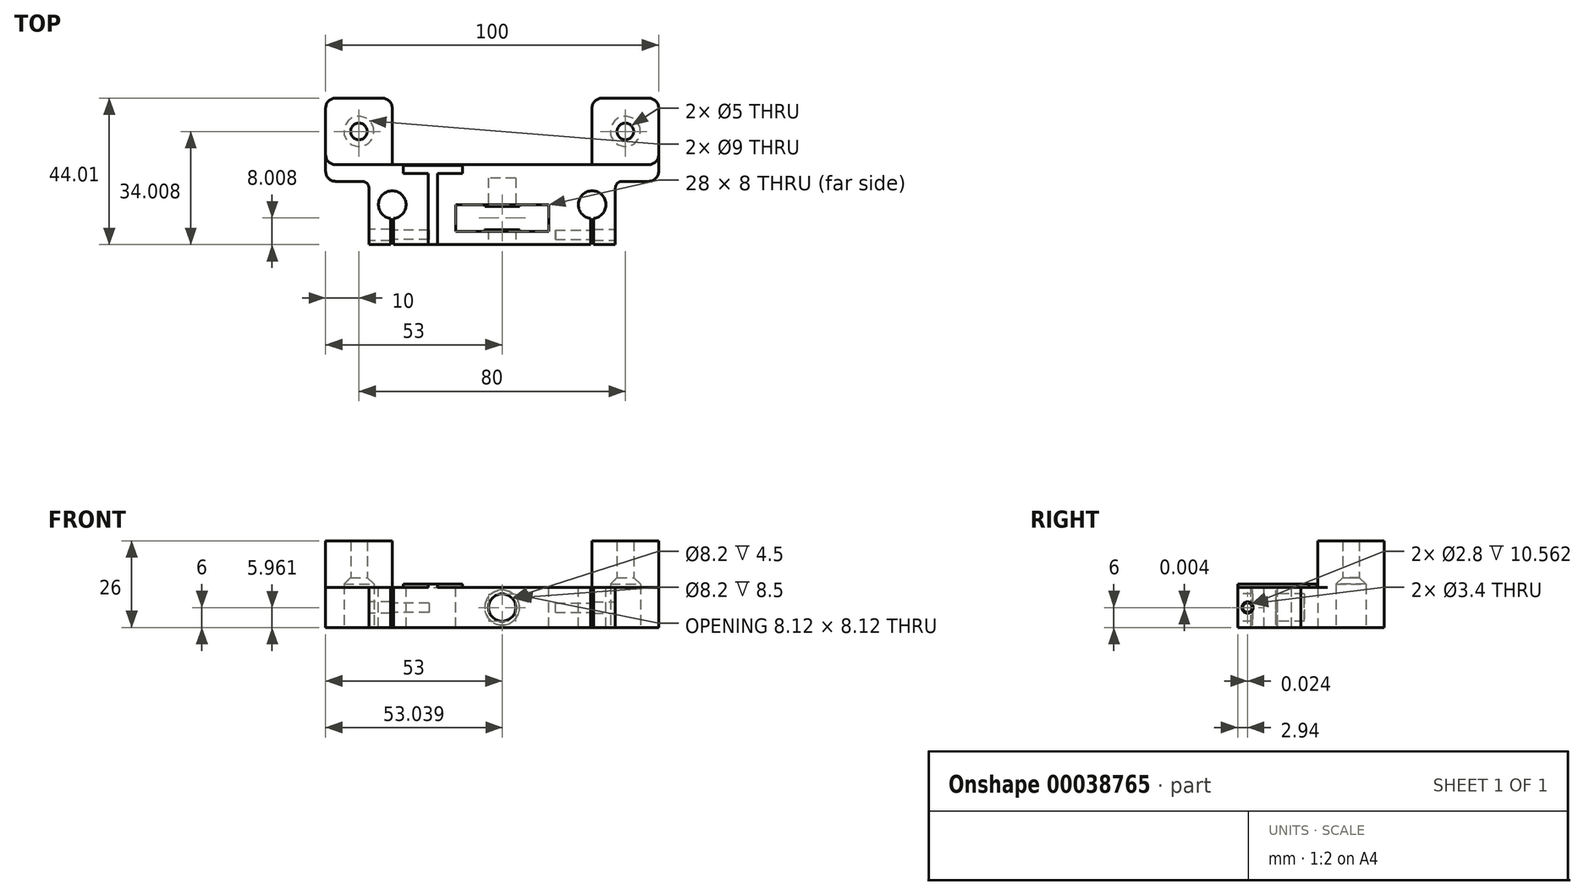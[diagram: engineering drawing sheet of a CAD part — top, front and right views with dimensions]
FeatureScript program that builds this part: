
annotation { "Feature Type Name" : "Feature", "Feature Type Description" : "" }
export const myFeature = defineFeature(function(context is Context, id is Id, definition is map)
    precondition{}
    {
        {
            var Q0;
            Q0=qCreatedBy(makeId("Top.planeOp"),FACE);
            var sketch = newSketch(context, id + "F0", { "sketchPlane" : qUnion([Q0])});
            skLineSegment(sketch, "E0", {"start": v(-46.35, 12.3) * mm, "end": v(53.65, 12.3) * mm});
            skLineSegment(sketch, "E1", {"start": v(53.65, 12.3) * mm, "end": v(53.65, 7.3) * mm});
            skLineSegment(sketch, "E2", {"start": v(53.65, 7.3) * mm, "end": v(40.65, 7.3) * mm});
            skLineSegment(sketch, "E3", {"start": v(40.65, 7.3) * mm, "end": v(40.65, -11.7) * mm});
            skLineSegment(sketch, "E4", {"start": v(40.65, -11.7) * mm, "end": v(-33.35, -11.7) * mm});
            skLineSegment(sketch, "E5", {"start": v(-33.35, -11.7) * mm, "end": v(-33.35, 7.3) * mm});
            skLineSegment(sketch, "E6", {"start": v(-33.35, 7.3) * mm, "end": v(-46.35, 7.3) * mm});
            skLineSegment(sketch, "E7", {"start": v(-46.35, 7.3) * mm, "end": v(-46.35, 12.3) * mm});
            skSolve(sketch);
        }
        {
            var Q0;
            Q0=qSketchRegion(id+"F0",true);
            extrude(context, id + "F1", {"entities" : qUnion([Q0]), "depth" : 12 * mm});
        }
        {
            var Q0;
            Q0=makeQuery(id+"F1.opExtrude","CAP_FACE",FACE,{"disambiguationData":[OSD([sQuery(id+"F0.wireOp",EDGE,"E0"),sQuery(id+"F0.wireOp",EDGE,"E1"),sQuery(id+"F0.wireOp",EDGE,"E2"),sQuery(id+"F0.wireOp",EDGE,"E3"),sQuery(id+"F0.wireOp",EDGE,"E4"),sQuery(id+"F0.wireOp",EDGE,"E5"),sQuery(id+"F0.wireOp",EDGE,"E6"),sQuery(id+"F0.wireOp",EDGE,"E7")])],"isStart":false});
            var sketch = newSketch(context, id + "F2", { "sketchPlane" : qUnion([Q0])});
            skCircle(sketch, "E8", {"center": v(-26.35, 0.3) * mm, "radius": 4.15 * mm});
            skCircle(sketch, "E9", {"center": v(33.65, 0.3) * mm, "radius": 4.15 * mm});
            skPoint(sketch, "E10", {"position": v(3.65, 12.3) * mm});
            skLineSegment(sketch, "E11.bottom", {"start": v(33.21, -3.01) * mm, "end": v(34.09, -3.01) * mm});
            skLineSegment(sketch, "E11.top", {"start": v(33.21, -12.27) * mm, "end": v(34.09, -12.27) * mm});
            skLineSegment(sketch, "E11.left", {"start": v(33.21, -3.01) * mm, "end": v(33.21, -12.27) * mm});
            skLineSegment(sketch, "E11.right", {"start": v(34.09, -3.01) * mm, "end": v(34.09, -12.27) * mm});
            skPoint(sketch, "E12", {"position": v(33.65, -3.01) * mm});
            skLineSegment(sketch, "E13", {"start": v(3.65, 12.3) * mm, "end": v(3.65, -11.7) * mm, "construction": true});
            skLineSegment(sketch, "E14.MirrorCS", {"start": v(-25.91, -12.27) * mm, "end": v(-26.79, -12.27) * mm});
            skLineSegment(sketch, "E15.MirrorCS", {"start": v(-26.79, -3.01) * mm, "end": v(-26.79, -12.27) * mm});
            skLineSegment(sketch, "E16.MirrorCS", {"start": v(-25.91, -3.01) * mm, "end": v(-26.79, -3.01) * mm});
            skLineSegment(sketch, "E17.MirrorCS", {"start": v(-25.91, -3.01) * mm, "end": v(-25.91, -12.27) * mm});
            skSolve(sketch);
        }
        {
            var Q0;
            Q0=qSketchRegion(id+"F2",true);
            var Q1;
            {var subQ3=sQuery(id+"F2.wireOp",EDGE,"E11.bottom");Q1=makeQuery(id+"F2.imprint","IMPRINT",FACE,{"disambiguationData":[TD([[makeQuery(id+"F2.imprint","IMPRINT",EDGE,{"derivedFrom":subQ3}),-1.0]])]});}
            var Q2;
            {var subQ3=sQuery(id+"F2.wireOp",EDGE,"E16.MirrorCS");Q2=makeQuery(id+"F2.imprint","IMPRINT",FACE,{"disambiguationData":[TD([[makeQuery(id+"F2.imprint","IMPRINT",EDGE,{"derivedFrom":subQ3}),1.0]])]});}
            extrude(context, id + "F3", {"entities" : qUnion([Q0, Q1, Q2]), "operationType" : NewBodyOperationType.REMOVE, "endBound" : BoundingType.THROUGH_ALL, "oppositeDirection" : true, "depth" : 25 * mm});
        }
        {
            var Q0;
            Q0=makeQuery(id+"F1.opExtrude","SWEPT_FACE",FACE,{"disambiguationData":[OSD([sQuery(id+"F0.wireOp",EDGE,"E4")])]});
            var sketch = newSketch(context, id + "F4", { "sketchPlane" : qUnion([Q0])});
            skLineSegment(sketch, "E18", {"start": v(-33.35, 6) * mm, "end": v(40.65, 6) * mm, "construction": true});
            skCircle(sketch, "E19", {"center": v(6.65, 6) * mm, "radius": 4.1 * mm});
            skSolve(sketch);
        }
        {
            var Q0;
            Q0=qSketchRegion(id+"F4",true);
            extrude(context, id + "F5", {"entities" : qUnion([Q0]), "operationType" : NewBodyOperationType.REMOVE, "oppositeDirection" : true, "depth" : 20 * mm});
        }
        {
            var Q0;
            Q0=makeQuery(id+"F1.opExtrude","CAP_FACE",FACE,{"disambiguationData":[OSD([sQuery(id+"F0.wireOp",EDGE,"E0"),sQuery(id+"F0.wireOp",EDGE,"E1"),sQuery(id+"F0.wireOp",EDGE,"E2"),sQuery(id+"F0.wireOp",EDGE,"E3"),sQuery(id+"F0.wireOp",EDGE,"E4"),sQuery(id+"F0.wireOp",EDGE,"E5"),sQuery(id+"F0.wireOp",EDGE,"E6"),sQuery(id+"F0.wireOp",EDGE,"E7")])],"isStart":false});
            var sketch = newSketch(context, id + "F6", { "sketchPlane" : qUnion([Q0])});
            skLineSegment(sketch, "E20.bottom", {"start": v(-7.35, 0.3) * mm, "end": v(20.65, 0.3) * mm});
            skLineSegment(sketch, "E20.top", {"start": v(-7.35, -7.7) * mm, "end": v(20.65, -7.7) * mm});
            skLineSegment(sketch, "E20.left", {"start": v(-7.35, 0.3) * mm, "end": v(-7.35, -7.7) * mm});
            skLineSegment(sketch, "E20.right", {"start": v(20.65, 0.3) * mm, "end": v(20.65, -7.7) * mm});
            skLineSegment(sketch, "E21", {"start": v(6.65, 12.3) * mm, "end": v(6.65, -11.7) * mm, "construction": true});
            skLineSegment(sketch, "E22", {"start": v(6.65, 0.3) * mm, "end": v(6.65, -7.7) * mm});
            skSolve(sketch);
        }
        {
            var Q0;
            Q0=qSketchRegion(id+"F6",true);
            extrude(context, id + "F7", {"entities" : qUnion([Q0]), "operationType" : NewBodyOperationType.REMOVE, "endBound" : BoundingType.THROUGH_ALL, "oppositeDirection" : true, "depth" : 25 * mm});
        }
        {
            var Q0;
            Q0=makeQuery(id+"F7.boolean.opBoolean","COPY",FACE,{"derivedFrom":makeQuery(id+"F7.opExtrude","SWEPT_FACE",FACE,{"disambiguationData":[OSD([sQuery(id+"F6.wireOp",EDGE,"E20.bottom")])]})});
            var sketch = newSketch(context, id + "F8", { "sketchPlane" : qUnion([Q0])});
            skCircle(sketch, "E23", {"center": v(6.65, 6) * mm, "radius": 5.2 * mm});
            skSolve(sketch);
        }
        {
            var Q0;
            Q0=makeQuery(id+"F8.imprint","IMPRINT",FACE,{"disambiguationData":[TD([[makeQuery(id+"F8.imprint","IMPRINT",EDGE,{"derivedFrom":sQuery(id+"F8.wireOp",EDGE,"E23")}),1.0]])]});
            extrude(context, id + "F9", {"entities" : qUnion([Q0]), "operationType" : NewBodyOperationType.ADD, "depth" : 0.5 * mm});
        }
        {
            var Q0;
            Q0=makeQuery(id+"F7.boolean.opBoolean","COPY",FACE,{"derivedFrom":makeQuery(id+"F7.opExtrude","SWEPT_FACE",FACE,{"disambiguationData":[OSD([sQuery(id+"F6.wireOp",EDGE,"E20.top")])]})});
            var sketch = newSketch(context, id + "F10", { "sketchPlane" : qUnion([Q0])});
            skCircle(sketch, "E24", {"center": v(-6.65, 6) * mm, "radius": 5.25 * mm});
            skSolve(sketch);
        }
        {
            var Q0;
            Q0=makeQuery(id+"F10.imprint","IMPRINT",FACE,{"disambiguationData":[TD([[makeQuery(id+"F10.imprint","IMPRINT",EDGE,{"derivedFrom":sQuery(id+"F10.wireOp",EDGE,"E24")}),1.0]])]});
            extrude(context, id + "F11", {"entities" : qUnion([Q0]), "operationType" : NewBodyOperationType.ADD, "depth" : 0.5 * mm});
        }
        {
            var Q0;
            Q0=makeQuery(id+"F1.opExtrude","CAP_FACE",FACE,{"disambiguationData":[OSD([sQuery(id+"F0.wireOp",EDGE,"E0"),sQuery(id+"F0.wireOp",EDGE,"E1"),sQuery(id+"F0.wireOp",EDGE,"E2"),sQuery(id+"F0.wireOp",EDGE,"E3"),sQuery(id+"F0.wireOp",EDGE,"E4"),sQuery(id+"F0.wireOp",EDGE,"E5"),sQuery(id+"F0.wireOp",EDGE,"E6"),sQuery(id+"F0.wireOp",EDGE,"E7")])],"isStart":false});
            var sketch = newSketch(context, id + "F12", { "sketchPlane" : qUnion([Q0])});
            skText(sketch, "E25", { "text": "T", "fontName": "OpenSans-Regular.ttf"});
            const initialGuessF12  = {"E25": [-0.02337, -0.0117, 1, 0, 0.024]};
            skSetInitialGuess(sketch, initialGuessF12);
            skSolve(sketch);
        }
        {
            var Q0;
            Q0=qSketchRegion(id+"F12",true);
            extrude(context, id + "F13", {"entities" : qUnion([Q0]), "operationType" : NewBodyOperationType.ADD, "depth" : 1 * mm});
        }
        {
            var Q0;
            Q0=makeQuery(id+"F1.opExtrude","SWEPT_FACE",FACE,{"disambiguationData":[OSD([sQuery(id+"F0.wireOp",EDGE,"E3")])]});
            var sketch = newSketch(context, id + "F14", { "sketchPlane" : qUnion([Q0])});
            skCircle(sketch, "E26", {"center": v(-8.74, 6) * mm, "radius": 1.7 * mm});
            skCircle(sketch, "E27", {"center": v(-8.74, 6) * mm, "radius": 1.4 * mm});
            skLineSegment(sketch, "E28", {"start": v(-11.7, 6) * mm, "end": v(-3.84, 6) * mm, "construction": true});
            skSolve(sketch);
        }
        {
            var Q0;
            Q0=makeQuery(id+"F14.imprint","IMPRINT",FACE,{"disambiguationData":[TD([[makeQuery(id+"F14.imprint","IMPRINT",EDGE,{"derivedFrom":sQuery(id+"F14.wireOp",EDGE,"E27")}),1.0]])]});
            extrude(context, id + "F15", {"entities" : qUnion([Q0]), "operationType" : NewBodyOperationType.REMOVE, "oppositeDirection" : true, "depth" : 18 * mm});
        }
        {
            var Q0;
            Q0=makeQuery(id+"F14.imprint","IMPRINT",FACE,{"disambiguationData":[TD([[makeQuery(id+"F14.imprint","IMPRINT",EDGE,{"derivedFrom":sQuery(id+"F14.wireOp",EDGE,"E27")}),1.0]])]});
            var Q1;
            Q1=makeQuery(id+"F14.imprint","IMPRINT",FACE,{"disambiguationData":[TD([[makeQuery(id+"F14.imprint","IMPRINT",EDGE,{"derivedFrom":sQuery(id+"F14.wireOp",EDGE,"E26")}),1.0]])]});
            extrude(context, id + "F16", {"entities" : qUnion([Q0, Q1]), "operationType" : NewBodyOperationType.REMOVE, "endBound" : BoundingType.UP_TO_NEXT, "oppositeDirection" : true, "depth" : 7 * mm});
        }
        {
            var Q0;
            Q0=makeQuery(id+"F1.opExtrude","SWEPT_EDGE",EDGE,{"disambiguationData":[OSD([sQuery(id+"F0.wireOp",EDGE,"E2"),sQuery(id+"F0.wireOp",EDGE,"E3")])]});
            fillet(context, id + "F17", {"entities" : qUnion([Q0]), "radius" : 2 * mm, "tangentPropagation" : true, "allowEdgeOverflow" : false});
        }
        {
            var Q0;
            Q0=makeQuery(id+"F1.opExtrude","SWEPT_FACE",FACE,{"disambiguationData":[OSD([sQuery(id+"F0.wireOp",EDGE,"E5")])]});
            var sketch = newSketch(context, id + "F18", { "sketchPlane" : qUnion([Q0])});
            skCircle(sketch, "E29", {"center": v(8.76, 6) * mm, "radius": 1.7 * mm});
            skCircle(sketch, "E30", {"center": v(8.76, 6) * mm, "radius": 1.4 * mm});
            skLineSegment(sketch, "E31", {"start": v(8.76, 0) * mm, "end": v(8.76, 12) * mm, "construction": true});
            skSolve(sketch);
        }
        {
            var Q0;
            Q0=makeQuery(id+"F18.imprint","IMPRINT",FACE,{"disambiguationData":[TD([[makeQuery(id+"F18.imprint","IMPRINT",EDGE,{"derivedFrom":sQuery(id+"F18.wireOp",EDGE,"E30")}),1.0]])]});
            extrude(context, id + "F19", {"entities" : qUnion([Q0]), "operationType" : NewBodyOperationType.REMOVE, "oppositeDirection" : true, "depth" : 18 * mm});
        }
        {
            var Q0;
            Q0=makeQuery(id+"F18.imprint","IMPRINT",FACE,{"disambiguationData":[TD([[makeQuery(id+"F18.imprint","IMPRINT",EDGE,{"derivedFrom":sQuery(id+"F18.wireOp",EDGE,"E30")}),1.0]])]});
            var Q1;
            Q1=makeQuery(id+"F18.imprint","IMPRINT",FACE,{"disambiguationData":[TD([[makeQuery(id+"F18.imprint","IMPRINT",EDGE,{"derivedFrom":sQuery(id+"F18.wireOp",EDGE,"E29")}),1.0]])]});
            extrude(context, id + "F20", {"entities" : qUnion([Q0, Q1]), "operationType" : NewBodyOperationType.REMOVE, "endBound" : BoundingType.UP_TO_NEXT, "oppositeDirection" : true, "depth" : 25 * mm});
        }
        {
            var Q0;
            Q0=makeQuery(id+"F1.opExtrude","SWEPT_EDGE",EDGE,{"disambiguationData":[OSD([sQuery(id+"F0.wireOp",EDGE,"E5"),sQuery(id+"F0.wireOp",EDGE,"E6")])]});
            fillet(context, id + "F21", {"entities" : qUnion([Q0]), "radius" : 2 * mm, "tangentPropagation" : true, "allowEdgeOverflow" : false});
        }
        {
            var Q0;
            Q0=makeQuery(id+"F1.opExtrude","SWEPT_FACE",FACE,{"disambiguationData":[OSD([sQuery(id+"F0.wireOp",EDGE,"E0")])]});
            var sketch = newSketch(context, id + "F22", { "sketchPlane" : qUnion([Q0])});
            skLineSegment(sketch, "E32.bottom", {"start": v(-53.65, 12) * mm, "end": v(-33.65, 12) * mm});
            skLineSegment(sketch, "E32.top", {"start": v(-53.65, 0) * mm, "end": v(-33.65, 0) * mm});
            skLineSegment(sketch, "E32.left", {"start": v(-53.65, 12) * mm, "end": v(-53.65, 0) * mm});
            skLineSegment(sketch, "E32.right", {"start": v(-33.65, 12) * mm, "end": v(-33.65, 0) * mm});
            skLineSegment(sketch, "E33.bottom", {"start": v(46.35, 12) * mm, "end": v(26.35, 12) * mm});
            skLineSegment(sketch, "E33.top", {"start": v(46.35, 0) * mm, "end": v(26.35, 0) * mm});
            skLineSegment(sketch, "E33.left", {"start": v(46.35, 12) * mm, "end": v(46.35, 0) * mm});
            skLineSegment(sketch, "E33.right", {"start": v(26.35, 12) * mm, "end": v(26.35, 0) * mm});
            skSolve(sketch);
        }
        {
            var Q0;
            Q0=qSketchRegion(id+"F22",true);
            extrude(context, id + "F23", {"entities" : qUnion([Q0]), "operationType" : NewBodyOperationType.ADD, "depth" : 20 * mm});
        }
        {
            var Q0;
            Q0=makeQuery(id+"F23.boolean.opBoolean","MERGE",FACE,{"derivedFrom":[makeQuery(id+"F1.opExtrude","CAP_FACE",FACE,{"disambiguationData":[OSD([sQuery(id+"F0.wireOp",EDGE,"E0"),sQuery(id+"F0.wireOp",EDGE,"E1"),sQuery(id+"F0.wireOp",EDGE,"E2"),sQuery(id+"F0.wireOp",EDGE,"E3"),sQuery(id+"F0.wireOp",EDGE,"E4"),sQuery(id+"F0.wireOp",EDGE,"E5"),sQuery(id+"F0.wireOp",EDGE,"E6"),sQuery(id+"F0.wireOp",EDGE,"E7")])],"isStart":false}),makeQuery(id+"F23.opExtrude","SWEPT_FACE",FACE,{"disambiguationData":[OSD([sQuery(id+"F22.wireOp",EDGE,"E32.bottom")])]}),makeQuery(id+"F23.opExtrude","SWEPT_FACE",FACE,{"disambiguationData":[OSD([sQuery(id+"F22.wireOp",EDGE,"E33.bottom")])]})]});
            var sketch = newSketch(context, id + "F24", { "sketchPlane" : qUnion([Q0])});
            skLineSegment(sketch, "E34.bottom", {"start": v(-46.35, 32.3) * mm, "end": v(-26.35, 32.3) * mm});
            skLineSegment(sketch, "E34.top", {"start": v(-46.35, 12.3) * mm, "end": v(-26.35, 12.3) * mm});
            skLineSegment(sketch, "E34.left", {"start": v(-46.35, 32.3) * mm, "end": v(-46.35, 12.3) * mm});
            skLineSegment(sketch, "E34.right", {"start": v(-26.35, 32.3) * mm, "end": v(-26.35, 12.3) * mm});
            skLineSegment(sketch, "E35.bottom", {"start": v(53.65, 32.3) * mm, "end": v(33.65, 32.3) * mm});
            skLineSegment(sketch, "E35.top", {"start": v(53.65, 12.3) * mm, "end": v(33.65, 12.3) * mm});
            skLineSegment(sketch, "E35.left", {"start": v(53.65, 32.3) * mm, "end": v(53.65, 12.3) * mm});
            skLineSegment(sketch, "E35.right", {"start": v(33.65, 32.3) * mm, "end": v(33.65, 12.3) * mm});
            skSolve(sketch);
        }
        {
            var Q0;
            Q0=qSketchRegion(id+"F24",true);
            extrude(context, id + "F25", {"entities" : qUnion([Q0]), "operationType" : NewBodyOperationType.ADD, "depth" : 14 * mm});
        }
        {
            var Q0;
            Q0=makeQuery(id+"F23.boolean.opBoolean","MERGE",FACE,{"derivedFrom":[makeQuery(id+"F1.opExtrude","CAP_FACE",FACE,{"disambiguationData":[OSD([sQuery(id+"F0.wireOp",EDGE,"E0"),sQuery(id+"F0.wireOp",EDGE,"E1"),sQuery(id+"F0.wireOp",EDGE,"E2"),sQuery(id+"F0.wireOp",EDGE,"E3"),sQuery(id+"F0.wireOp",EDGE,"E4"),sQuery(id+"F0.wireOp",EDGE,"E5"),sQuery(id+"F0.wireOp",EDGE,"E6"),sQuery(id+"F0.wireOp",EDGE,"E7")])],"isStart":true}),makeQuery(id+"F23.opExtrude","SWEPT_FACE",FACE,{"disambiguationData":[OSD([sQuery(id+"F22.wireOp",EDGE,"E32.top")])]}),makeQuery(id+"F23.opExtrude","SWEPT_FACE",FACE,{"disambiguationData":[OSD([sQuery(id+"F22.wireOp",EDGE,"E33.top")])]})]});
            var sketch = newSketch(context, id + "F26", { "sketchPlane" : qUnion([Q0])});
            skCircle(sketch, "E36", {"center": v(-36.35, -22.3) * mm, "radius": 2.5 * mm});
            skCircle(sketch, "E37", {"center": v(43.65, -22.3) * mm, "radius": 2.5 * mm});
            skPoint(sketch, "E38", {"position": v(-36.35, -32.3) * mm});
            skPoint(sketch, "E39", {"position": v(43.65, -32.3) * mm});
            skCircle(sketch, "E40", {"center": v(-36.35, -22.3) * mm, "radius": 4.5 * mm});
            skCircle(sketch, "E41", {"center": v(43.65, -22.3) * mm, "radius": 4.5 * mm});
            skSolve(sketch);
        }
        {
            var Q0;
            Q0=makeQuery(id+"F26.imprint","IMPRINT",FACE,{"disambiguationData":[TD([[makeQuery(id+"F26.imprint","IMPRINT",EDGE,{"derivedFrom":sQuery(id+"F26.wireOp",EDGE,"E36")}),1.0]])]});
            var Q1;
            Q1=makeQuery(id+"F26.imprint","IMPRINT",FACE,{"disambiguationData":[TD([[makeQuery(id+"F26.imprint","IMPRINT",EDGE,{"derivedFrom":sQuery(id+"F26.wireOp",EDGE,"E37")}),1.0]])]});
            extrude(context, id + "F27", {"entities" : qUnion([Q0, Q1]), "operationType" : NewBodyOperationType.REMOVE, "endBound" : BoundingType.THROUGH_ALL, "oppositeDirection" : true, "depth" : 25 * mm});
        }
        {
            var Q0;
            Q0=makeQuery(id+"F1.opExtrude","SWEPT_EDGE",EDGE,{"disambiguationData":[OSD([sQuery(id+"F0.wireOp",EDGE,"E6"),sQuery(id+"F0.wireOp",EDGE,"E7")])]});
            var Q1;
            Q1=makeQuery(id+"F23.opExtrude","CAP_EDGE",EDGE,{"disambiguationData":[OSD([sQuery(id+"F22.wireOp",EDGE,"E33.left")])],"isStart":false});
            var Q2;
            Q2=makeQuery(id+"F23.opExtrude","CAP_EDGE",EDGE,{"disambiguationData":[OSD([sQuery(id+"F22.wireOp",EDGE,"E33.right")])],"isStart":false});
            var Q3;
            Q3=makeQuery(id+"F23.opExtrude","CAP_EDGE",EDGE,{"disambiguationData":[OSD([sQuery(id+"F22.wireOp",EDGE,"E33.right")])],"isStart":true});
            var Q4;
            Q4=makeQuery(id+"F23.opExtrude","CAP_EDGE",EDGE,{"disambiguationData":[OSD([sQuery(id+"F22.wireOp",EDGE,"E32.right")])],"isStart":true});
            var Q5;
            Q5=makeQuery(id+"F23.opExtrude","CAP_EDGE",EDGE,{"disambiguationData":[OSD([sQuery(id+"F22.wireOp",EDGE,"E32.right")])],"isStart":false});
            var Q6;
            Q6=makeQuery(id+"F23.opExtrude","CAP_EDGE",EDGE,{"disambiguationData":[OSD([sQuery(id+"F22.wireOp",EDGE,"E32.left")])],"isStart":false});
            var Q7;
            Q7=makeQuery(id+"F1.opExtrude","SWEPT_EDGE",EDGE,{"disambiguationData":[OSD([sQuery(id+"F0.wireOp",EDGE,"E1"),sQuery(id+"F0.wireOp",EDGE,"E2")])]});
            var Q8;
            Q8=makeQuery(id+"F25.opExtrude","SWEPT_EDGE",EDGE,{"disambiguationData":[OSD([sQuery(id+"F0.wireOp",EDGE,"E7"),sQuery(id+"F22.wireOp",EDGE,"E33.bottom"),sQuery(id+"F22.wireOp",EDGE,"E33.left"),sQuery(id+"F24.wireOp",EDGE,"E34.top"),sQuery(id+"F24.wireOp",EDGE,"E34.left")])]});
            var Q9;
            Q9=makeQuery(id+"F25.opExtrude","SWEPT_EDGE",EDGE,{"disambiguationData":[OSD([sQuery(id+"F0.wireOp",EDGE,"E1"),sQuery(id+"F22.wireOp",EDGE,"E32.bottom"),sQuery(id+"F22.wireOp",EDGE,"E32.left"),sQuery(id+"F24.wireOp",EDGE,"E35.top"),sQuery(id+"F24.wireOp",EDGE,"E35.left")])]});
            fillet(context, id + "F28", {"entities" : qUnion([Q0, Q1, Q2, Q3, Q4, Q5, Q6, Q7, Q8, Q9]), "radius" : 3 * mm, "tangentPropagation" : true, "allowEdgeOverflow" : false});
        }
        {
            var Q0;
            Q0=makeQuery(id+"F26.imprint","IMPRINT",FACE,{"disambiguationData":[TD([[makeQuery(id+"F26.imprint","IMPRINT",EDGE,{"derivedFrom":sQuery(id+"F26.wireOp",EDGE,"E36")}),-1.0]])]});
            var Q1;
            Q1=makeQuery(id+"F26.imprint","IMPRINT",FACE,{"disambiguationData":[TD([[makeQuery(id+"F26.imprint","IMPRINT",EDGE,{"derivedFrom":sQuery(id+"F26.wireOp",EDGE,"E37")}),-1.0]])]});
            extrude(context, id + "F29", {"entities" : qUnion([Q0, Q1]), "operationType" : NewBodyOperationType.REMOVE, "oppositeDirection" : true, "depth" : 16 * mm});
        }
        {
            var Q0;
            Q0=makeQuery(id+"F29.boolean.opBoolean","COPY",EDGE,{"derivedFrom":makeQuery(id+"F29.opExtrude","CAP_EDGE",EDGE,{"disambiguationData":[OSD([sQuery(id+"F26.wireOp",EDGE,"E40")])],"isStart":false})});
            var Q1;
            Q1=makeQuery(id+"F29.boolean.opBoolean","COPY",EDGE,{"derivedFrom":makeQuery(id+"F29.opExtrude","CAP_EDGE",EDGE,{"disambiguationData":[OSD([sQuery(id+"F26.wireOp",EDGE,"E41")])],"isStart":false})});
            chamfer(context, id + "F30", {"entities" : qUnion([Q0, Q1]), "width" : 3 * mm, "tangentPropagation" : true});
        }
    });
